# Revit family: Benches-Bernhardt_Design-Apel
name_source: partatom
category: Furniture
revit_build: Autodesk Revit Architecture 2013 (Build: 20130531_2115(x64)
units: mm (PartAtom-declared; Revit-internal decimal feet)

## types (6) — shared parameters
Base Finish = Plastic - Bernhardt Design - Black
Description = Ottoman
Manufacturer = Bernhardt Design
Product Documentation Link = http://bernhardtdesign.com
Product Name = Apel
Product Page URL = http://bernhardtdesign.com
Seat Height = 1' - 5 1/4"
URL = http://bernhardtdesign.com
Upholstery = Fabric- Bernhardt Design - Orange Linen

## per-type parameters (varying)
| type | Casters | Depth | Detail Line Constraint | Detail Line Constraint 2 | Height | Masking Region Constraint | Model | Stitch | Stitch Constraint | Width |
| 5850 - Saddle Stitch | No | 1' - 10 1/4" | 0' - 9 21/32" | 0' - 9 25/32" | 1' - 4 1/2" | 0' - 11 1/8" | 5850 | Fabric- Bernhardt Design - Orange Linen | 0' - 6 23/32" | 1' - 10 1/4" |
| 5850L - Loop Master Stitch | No | 1' - 10 1/4" | 0' - 9 21/32" | 0' - 9 25/32" | 1' - 4 1/2" | 0' - 11 1/8" | 5850L | Fabric- Bernhardt Design - Loop Master Stitch | 0' - 6 23/32" | 1' - 10 1/4" |
| 5850M - Saddle Stitch - Mobile | Yes | 1' - 10 1/4" | 0' - 9 21/32" | 0' - 9 25/32" | 1' - 5 1/2" | 0' - 11 1/8" | 5850M | Fabric- Bernhardt Design - Orange Linen | 0' - 6 23/32" | 1' - 10 1/4" |
| 5850ML - Loop Master Stitch - Mobile | Yes | 1' - 10 1/4" | 0' - 9 21/32" | 0' - 9 25/32" | 1' - 5 1/2" | 0' - 11 1/8" | 5850ML | Fabric- Bernhardt Design - Loop Master Stitch | 0' - 6 23/32" | 1' - 10 1/4" |
| 5851 - Saddle Stitch | No | 3' - 5 1/4" | 1' - 7 5/32" | 1' - 7 9/32" | 1' - 4 1/2" | 1' - 8 5/8" | 5851 | Fabric- Bernhardt Design - Orange Linen | 1' - 1 11/16" | 3' - 5 1/4" |
| 5851L - Loop Master Stitch | No | 3' - 5 1/4" | 1' - 7 5/32" | 1' - 7 9/32" | 1' - 4 1/2" | 1' - 8 5/8" | 5851L | Fabric- Bernhardt Design - Loop Master Stitch | 1' - 1 11/16" | 3' - 5 1/4" |

## geometry (parser evidence)
native form markers: Blend x49, Sweep x2
no freeform markers — native parametric forms only
